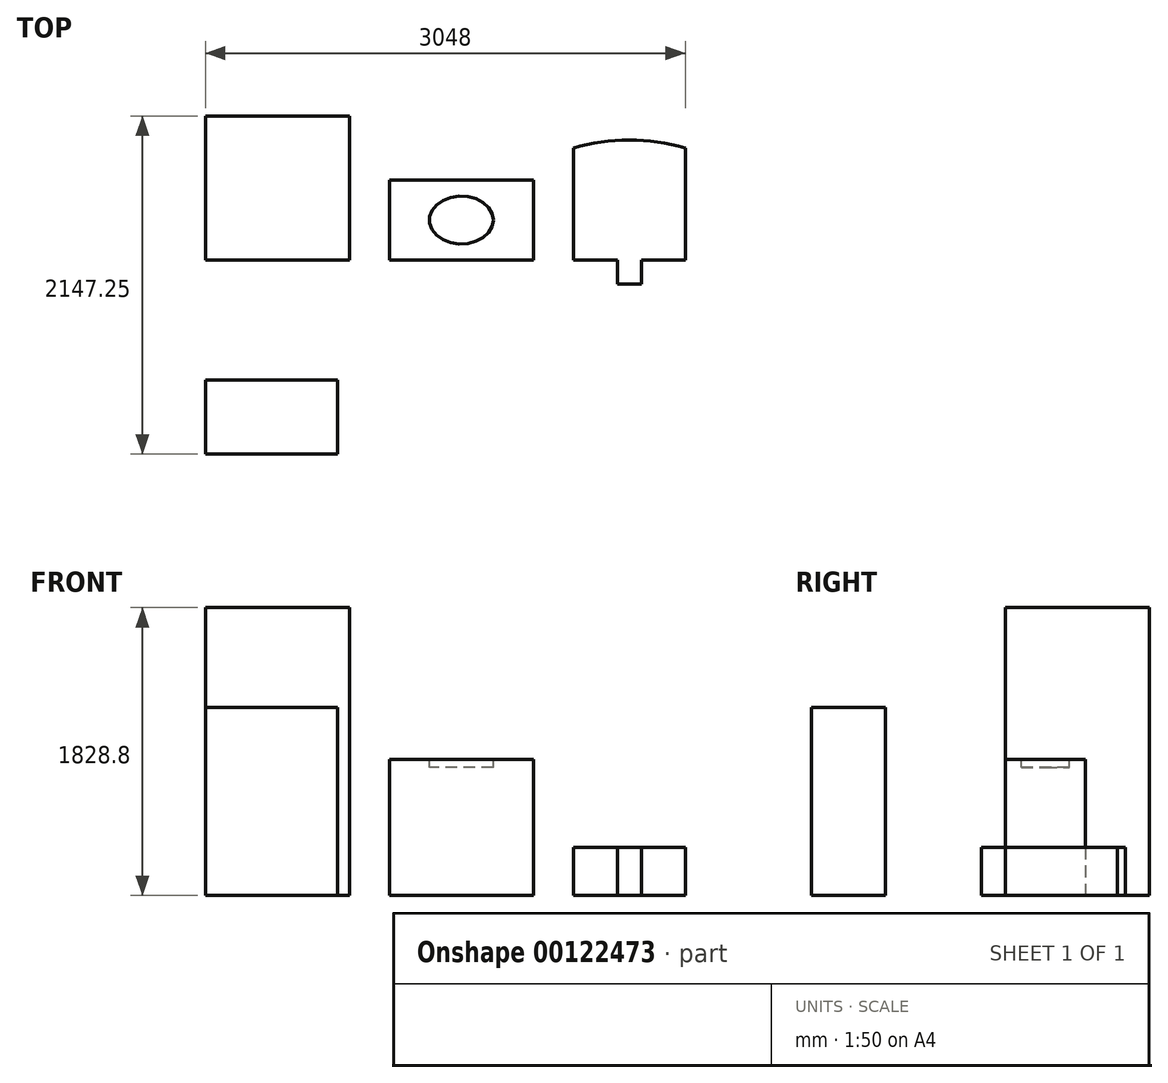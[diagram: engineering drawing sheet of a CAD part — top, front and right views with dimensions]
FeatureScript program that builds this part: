
annotation { "Feature Type Name" : "Feature", "Feature Type Description" : "" }
export const myFeature = defineFeature(function(context is Context, id is Id, definition is map)
    precondition{}
    {
        {
            var Q0;
            Q0=qCreatedBy(makeId("Top.planeOp"),FACE);
            var sketch = newSketch(context, id + "F0", { "sketchPlane" : qUnion([Q0])});
            skLineSegment(sketch, "E0.bottom", {"start": v(0, 0) * mm, "end": v(914.4, 0) * mm});
            skLineSegment(sketch, "E0.top", {"start": v(0, 914.4) * mm, "end": v(914.4, 914.4) * mm});
            skLineSegment(sketch, "E0.left", {"start": v(0, 0) * mm, "end": v(0, 914.4) * mm});
            skLineSegment(sketch, "E0.right", {"start": v(914.4, 0) * mm, "end": v(914.4, 914.4) * mm});
            skSolve(sketch);
        }
        {
            var Q0;
            Q0 = qSketchRegion(id + "F0", true);
            extrude(context, id + "F1", {"entities" : qUnion([Q0]), "depth" : 1828.8 * mm, "offsetDistance" : 25.4 * mm});
        }
        {
            var Q0;
            Q0=qCreatedBy(makeId("Top.planeOp"),FACE);
            var sketch = newSketch(context, id + "F2", { "sketchPlane" : qUnion([Q0])});
            skLineSegment(sketch, "E1.bottom", {"start": v(1168.4, 0) * mm, "end": v(2082.8, 0) * mm});
            skLineSegment(sketch, "E1.top", {"start": v(1168.4, 508) * mm, "end": v(2082.8, 508) * mm});
            skLineSegment(sketch, "E1.left", {"start": v(1168.4, 0) * mm, "end": v(1168.4, 508) * mm});
            skLineSegment(sketch, "E1.right", {"start": v(2082.8, 0) * mm, "end": v(2082.8, 508) * mm});
            skSolve(sketch);
        }
        {
            var Q0;
            Q0 = qSketchRegion(id + "F2", true);
            extrude(context, id + "F3", {"entities" : qUnion([Q0]), "depth" : 863.6 * mm, "offsetDistance" : 25.4 * mm});
        }
        {
            var Q0;
            Q0=makeQuery(id+"F3.opExtrude","CAP_FACE",FACE,{"disambiguationData":[OSD([sQuery(id+"F2.wireOp",EDGE,"E1.bottom"),sQuery(id+"F2.wireOp",EDGE,"E1.top"),sQuery(id+"F2.wireOp",EDGE,"E1.left"),sQuery(id+"F2.wireOp",EDGE,"E1.right")])],"isStart":false});
            var sketch = newSketch(context, id + "F4", { "sketchPlane" : qUnion([Q0])});
            skLineSegment(sketch, "E2", {"start": v(1625.6, 508) * mm, "end": v(1625.6, 0) * mm});
            skEllipse(sketch, "E3", {"center": v(1625.6, 254) * mm, "majorRadius": 203.2 * mm, "minorRadius": 152.4 * mm, "majorAxis": v(1, 0)});
            skLineSegment(sketch, "E4", {"start": v(1422.4, 254) * mm, "end": v(1828.8, 254) * mm});
            skPoint(sketch, "E4.startSnap0", {"position": v(1422.4, 254) * mm});
            skSolve(sketch);
        }
        {
            var Q0;
            Q0 = qSketchRegion(id + "F4", true);
            extrude(context, id + "F5", {"entities" : qUnion([Q0]), "operationType" : NewBodyOperationType.REMOVE, "oppositeDirection" : true, "depth" : 50.8 * mm, "offsetDistance" : 25.4 * mm});
        }
        {
            var Q0;
            Q0=qCreatedBy(makeId("Top.planeOp"),FACE);
            var sketch = newSketch(context, id + "F6", { "sketchPlane" : qUnion([Q0])});
            skLineSegment(sketch, "E5.left", {"start": v(2336.8, 0) * mm, "end": v(2336.8, 711.2) * mm});
            skLineSegment(sketch, "E5.right", {"start": v(3048, 0) * mm, "end": v(3048, 711.2) * mm});
            skLineSegment(sketch, "E6", {"start": v(2336.8, 0) * mm, "end": v(2616.2, 0) * mm});
            skLineSegment(sketch, "E7", {"start": v(2616.2, 0) * mm, "end": v(2616.2, -152.4) * mm});
            skLineSegment(sketch, "E8", {"start": v(2616.2, -152.4) * mm, "end": v(2768.6, -152.4) * mm});
            skLineSegment(sketch, "E9", {"start": v(2768.6, -152.4) * mm, "end": v(2768.6, 0) * mm});
            skLineSegment(sketch, "E10", {"start": v(2768.6, 0) * mm, "end": v(3048, 0) * mm});
            skArc(sketch, "E11", {"start": v(3048, 711.2) * mm, "mid": v(2692.4, 762) * mm, "end": v(2336.8, 711.2) * mm});
            skLineSegment(sketch, "E12", {"start": v(2692.4, 762) * mm, "end": v(2692.4, -152.4) * mm});
            skSolve(sketch);
        }
        {
            var Q0;
            Q0 = qSketchRegion(id + "F6", true);
            extrude(context, id + "F7", {"entities" : qUnion([Q0]), "depth" : 304.8 * mm, "offsetDistance" : 25.4 * mm});
        }
        {
            var Q0;
            Q0=qCreatedBy(makeId("Top.planeOp"), FACE);
            var sketch = newSketch(context, id + "F8", { "sketchPlane" : qUnion([Q0])});
            skLineSegment(sketch, "E13.bottom", {"start": v(0, -1232.85) * mm, "end": v(838.2, -1232.85) * mm});
            skLineSegment(sketch, "E13.top", {"start": v(0, -762.95) * mm, "end": v(838.2, -762.95) * mm});
            skLineSegment(sketch, "E13.left", {"start": v(0, -1232.85) * mm, "end": v(0, -762.95) * mm});
            skLineSegment(sketch, "E13.right", {"start": v(838.2, -1232.85) * mm, "end": v(838.2, -762.95) * mm});
            skSolve(sketch);
        }
        {
            var Q0;
            Q0 = qSketchRegion(id + "F8", true);
            extrude(context, id + "F9", {"entities" : qUnion([Q0]), "domain" : OperationDomain.MODEL, "flatOperationType" : FlatOperationType.REMOVE, "depth" : 1193.8 * mm, "offsetDistance" : 25.4 * mm});
        }
    });
